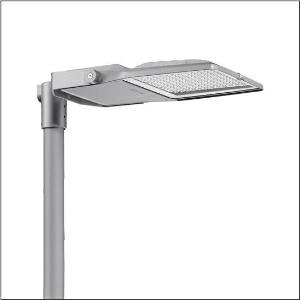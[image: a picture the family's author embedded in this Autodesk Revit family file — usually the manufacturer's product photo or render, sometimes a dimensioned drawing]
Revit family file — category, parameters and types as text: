
# Revit family: floodlight_fl_21_iq_midi___pl64_5xa7782e2e3a_fffa
name_source: partatom
category: Lighting Fixtures
units: mm (PartAtom-declared; Revit-internal decimal feet)

## family parameters
Cut with Voids When Loaded = No
Host = Face
Light Source = No
Part Type = Normal
Room Calculation Point = No
Round Connector Dimension = Use Diameter
Shared = No

## types (1)
- --- (1 x LED, 25930 lm, 208.1 W, 3000K)
    Apparent Load = 208 VA
    CIE Flux Codes = 28 80 98 100 100
    Color Rendering = 70
    Color Temperature = 3000K
    Default Elevation = 1800 mm
    Description = Floodlight FL 21 iQ midi, floodlight, primary light control with lens, of PMMA, primary optical cover: protective disc, of toughened safety glass, transparent, light distribution: PL64, light emission: direct distribution, installation type: surface-mounted, LED, High Power LED, rated luminous flux: 25.930lm, luminous efficacy: 125lm/W, light colour: 730, colour temperature: 3000K, control gear: ECG iQ, control: optimised constant luminous flux control (CLO 2.0), Desk-Remote (wireless, voltage-free reading and setting of iQ features in the workshop via application-optimized NFC function/RFID function), Smart-Wire, Night-Set, Temp-Guard, Auto-Match, Street-Remote, with terminal, 6-pole, mains connection: 220..240V, AC, 50/60Hz, start of lifetime: 208W, end of service life: 227W, reduction: 90W, luminaire housing, of diecast aluminium, powder-coated, Siteco® metallic grey (DB 702S), corrosivity category C5 mid according to DIN EN ISO 12944, sealing non-destructively replaceable, please order mast flange separately, mast bracket, of steel, galvanised, powder-coated, Siteco® metallic grey (DB 702S), protection rating (complete): IP66, insulation class (complete): insulation class II (safety insulation), certification: CE, protection symbol: D, impact resistance: IK08, permissible operating ambient temperature: -40..+40°C, permissible operating ambient temperature for outdoor applications: -40..+50°C, standard: DIN EN 12944, LABS conformity tested according to VDMA 24364:2018-05, packaging unit: 1 piece

Light Distribution: PL64
    Height = 76 mm
    Lamp = 1 x LED
    Lamp Light Flux = 25930 lm
    Lamp Power = 208.1 W
    Lamp count = 1
    Length = 657 mm
    Luminous efficacy = 125 lm/W
    Manufacturer = Siteco
    ModVariant = No
    Model = 5XA7782E2E3A
    Number of Poles = 1
    OnlyDefault = Yes
    Power Factor = 1
    Product Name = Floodlight FL 21 iQ midi | PL64
    Product group = floodlight | pylon annexe
    ProductGroupID = 6200
    Protection Class = Protection class II
    Protection Degree = IP 66
    RLX_Detail_Level = 1
    RLX_Emergency_Light_Flux = 0 lm
    RLX_Emergency_Type = 0
    RLX_Emergency_Type_DB = No
    RlxData = <blob elided: 153581 chars, md5=8af03182>
    Socket = socket
    Standby Power = 0 W
    System Light Flux = 25930 lm
    System Power = 208 W
    Type Comments = factory setting: luminous flux: 100 % | dim-lin: 254 | 710 mA
    Type Image = l_1007123.jpg
    URL = http://relux.com
    VarID = @adj_037223
    Voltage = 0 V
    Weight = 0.00 kg
    Width = 442 mm

## geometry (parser evidence)
native form markers: Blend x4, Sweep x14
no freeform markers — native parametric forms only
